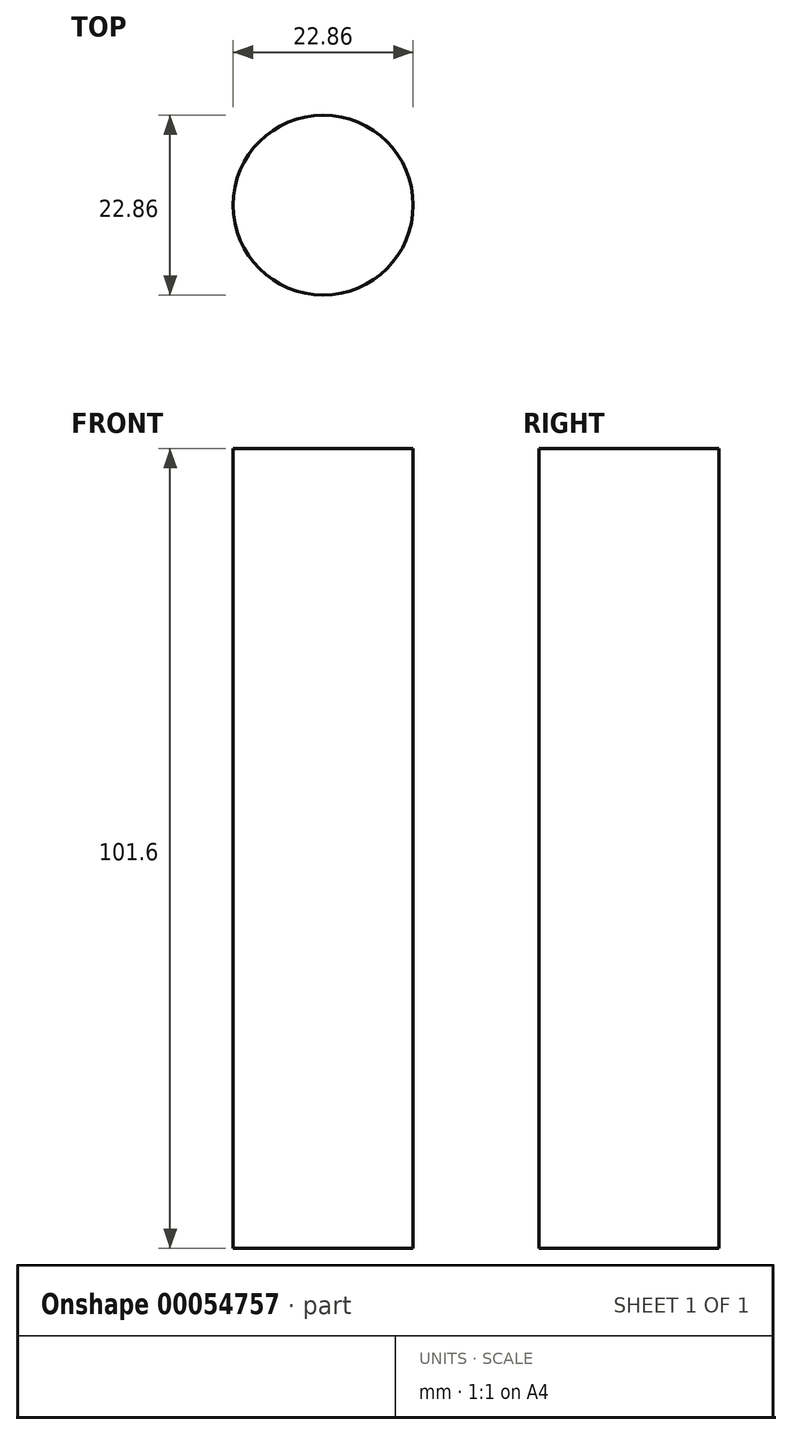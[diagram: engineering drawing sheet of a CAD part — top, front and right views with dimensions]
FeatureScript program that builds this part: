
annotation { "Feature Type Name" : "Feature", "Feature Type Description" : "" }
export const myFeature = defineFeature(function(context is Context, id is Id, definition is map)
    precondition{}
    {
        {
            var Q0;
            Q0=qCreatedBy(makeId("Top.planeOp"),FACE);
            var sketch = newSketch(context, id + "F0", { "sketchPlane" : qUnion([Q0])});
            skCircle(sketch, "E0", {"center": v(0, 0) * mm, "radius": 11.43 * mm});
            skSolve(sketch);
        }
        {
            var Q0;
            Q0=makeQuery(id+"F0.imprint","IMPRINT",FACE,{"disambiguationData":[TD([[makeQuery(id+"F0.imprint","IMPRINT",EDGE,{"derivedFrom":sQuery(id+"F0.wireOp",EDGE,"E0")}),1.0]])]});
            extrude(context, id + "F1", {"entities" : qUnion([Q0]), "depth" : 101.6 * mm});
        }
    });
